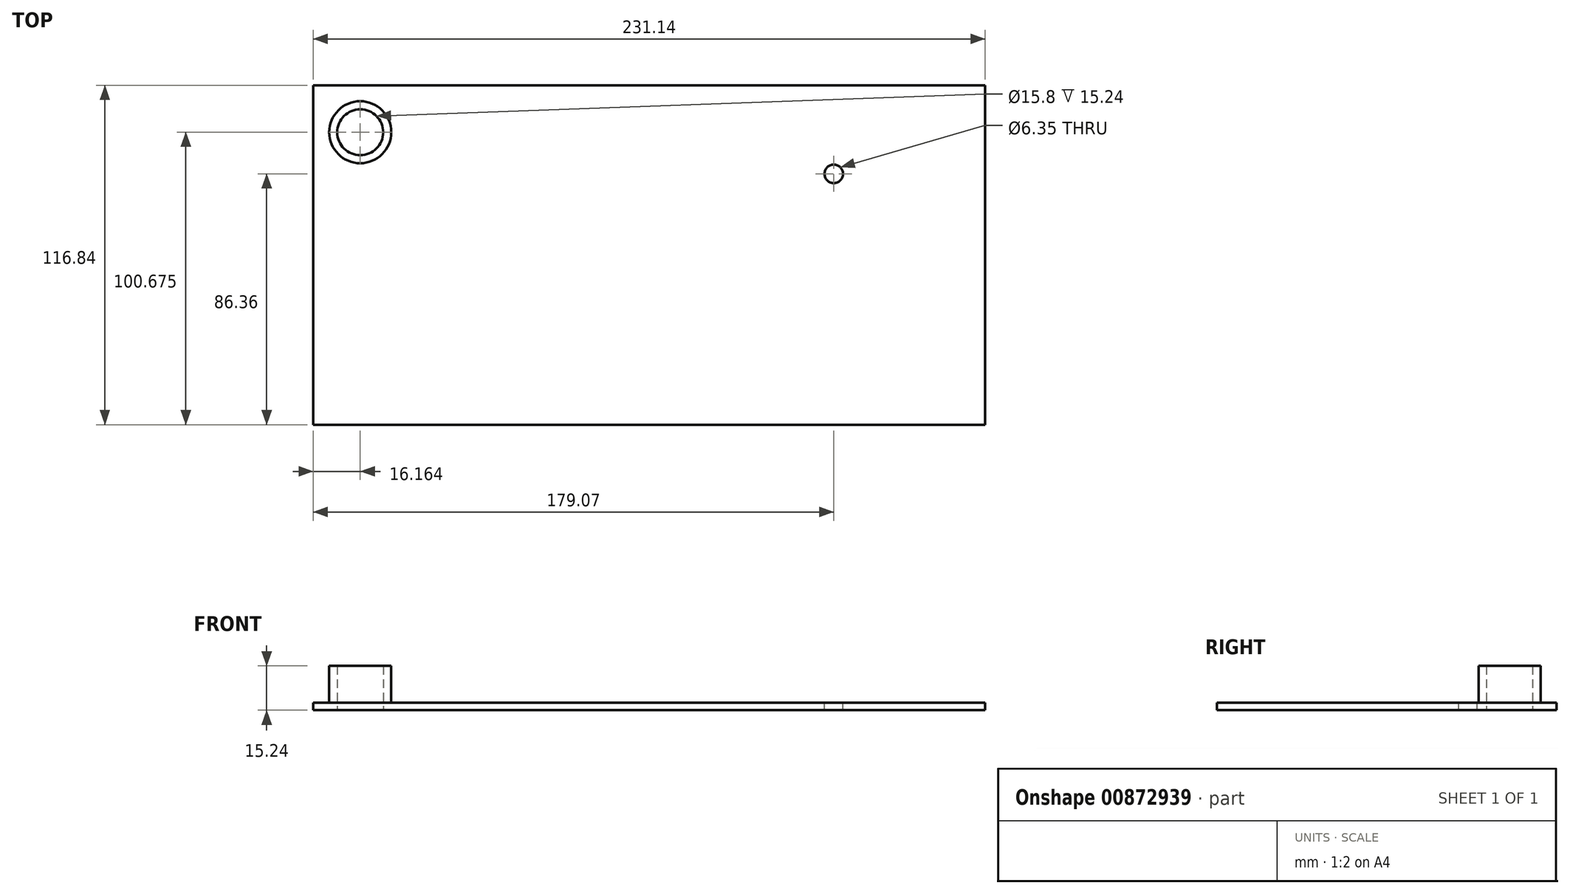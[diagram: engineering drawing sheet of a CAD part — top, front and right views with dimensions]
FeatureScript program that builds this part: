
annotation { "Feature Type Name" : "Feature", "Feature Type Description" : "" }
export const myFeature = defineFeature(function(context is Context, id is Id, definition is map)
    precondition{}
    {
        {
            var Q0;
            Q0=qCreatedBy(makeId("Top.planeOp"),FACE);
            var sketch = newSketch(context, id + "F0", { "sketchPlane" : qUnion([Q0])});
            skLineSegment(sketch, "E0.bottom", {"start": v(115.57, 58.42) * mm, "end": v(-115.57, 58.42) * mm});
            skLineSegment(sketch, "E0.top", {"start": v(115.57, -58.42) * mm, "end": v(-115.57, -58.42) * mm});
            skLineSegment(sketch, "E0.left", {"start": v(115.57, 58.42) * mm, "end": v(115.57, -58.42) * mm});
            skLineSegment(sketch, "E0.right", {"start": v(-115.57, 58.42) * mm, "end": v(-115.57, -58.42) * mm});
            skPoint(sketch, "E0.middle", {"position": v(0, 0) * mm});
            skSolve(sketch);
        }
        {
            var Q0;
            Q0=makeQuery(id+"F0.imprint","IMPRINT",FACE,{"disambiguationData":[TD([[makeQuery(id+"F0.imprint","IMPRINT",EDGE,{"derivedFrom":sQuery(id+"F0.wireOp",EDGE,"E0.bottom")}),1.0]])]});
            extrude(context, id + "F1", {"entities" : qUnion([Q0]), "depth" : 2.54 * mm, "offsetDistance" : 25.4 * mm});
        }
        {
            var Q0;
            Q0=makeQuery(id+"F1.opExtrude","CAP_FACE",FACE,{"disambiguationData":[OSD([sQuery(id+"F0.wireOp",EDGE,"E0.bottom"),sQuery(id+"F0.wireOp",EDGE,"E0.top"),sQuery(id+"F0.wireOp",EDGE,"E0.left"),sQuery(id+"F0.wireOp",EDGE,"E0.right")])],"isStart":false});
            var sketch = newSketch(context, id + "F2", { "sketchPlane" : qUnion([Q0])});
            skLineSegment(sketch, "E1", {"start": v(-115.57, 58.42) * mm, "end": v(-99.4, 42.26) * mm});
            skCircle(sketch, "E2", {"center": v(-99.4, 42.26) * mm, "radius": 7.9 * mm});
            skCircle(sketch, "E3", {"center": v(-99.4, 42.26) * mm, "radius": 10.67 * mm});
            skSolve(sketch);
        }
        {
            var Q0;
            Q0=makeQuery(id+"F2.imprint","IMPRINT",FACE,{"disambiguationData":[TD([[makeQuery(id+"F2.imprint","IMPRINT",EDGE,{"derivedFrom":sQuery(id+"F2.wireOp",EDGE,"E2")}),-1.0]])]});
            extrude(context, id + "F3", {"entities" : qUnion([Q0]), "operationType" : NewBodyOperationType.ADD, "depth" : 12.7 * mm, "offsetDistance" : 25.4 * mm});
        }
        {
            var Q0;
            Q0=makeQuery(id+"F3.boolean.opBoolean","SPLIT",FACE,{"disambiguationData":[TD([makeQuery(id+"F3.opExtrude","SWEPT_FACE",FACE,{"disambiguationData":[OSD([sQuery(id+"F2.wireOp",EDGE,"E2")])]})])],"derivedFrom":makeQuery(id+"F1.opExtrude","CAP_FACE",FACE,{"disambiguationData":[OSD([sQuery(id+"F0.wireOp",EDGE,"E0.bottom"),sQuery(id+"F0.wireOp",EDGE,"E0.top"),sQuery(id+"F0.wireOp",EDGE,"E0.left"),sQuery(id+"F0.wireOp",EDGE,"E0.right")])],"isStart":false})});
            var sketch = newSketch(context, id + "F4", { "sketchPlane" : qUnion([Q0])});
            skCircle(sketch, "E4", {"center": v(-99.4, 42.26) * mm, "radius": 7.9 * mm});
            skSolve(sketch);
        }
        {
            var Q0;
            Q0=makeQuery(id+"F4.imprint","IMPRINT",FACE,{"disambiguationData":[TD([[makeQuery(id+"F4.imprint","IMPRINT",EDGE,{"derivedFrom":sQuery(id+"F4.wireOp",EDGE,"E4")}),1.0]])]});
            var Q1;
            Q1=makeQuery(id+"F1.opExtrude","CAP_FACE",FACE,{"disambiguationData":[OSD([sQuery(id+"F0.wireOp",EDGE,"E0.bottom"),sQuery(id+"F0.wireOp",EDGE,"E0.top"),sQuery(id+"F0.wireOp",EDGE,"E0.left"),sQuery(id+"F0.wireOp",EDGE,"E0.right")])],"isStart":true});
            extrude(context, id + "F5", {"entities" : qUnion([Q0]), "operationType" : NewBodyOperationType.REMOVE, "endBound" : BoundingType.UP_TO_SURFACE, "oppositeDirection" : true, "depth" : 25.4 * mm, "endBoundEntityFace" : qUnion([Q1]), "offsetDistance" : 25.4 * mm});
        }
        {
            var Q0;
            {var subQ0=sQuery(id+"F0.wireOp",EDGE,"E0.left");var subQ4=sQuery(id+"F0.wireOp",EDGE,"E0.top");var subQ6=sQuery(id+"F0.wireOp",EDGE,"E0.right");var subQ8=sQuery(id+"F0.wireOp",EDGE,"E0.bottom");var subQ9=makeQuery(id+"F1.opExtrude","SWEPT_FACE",FACE,{"disambiguationData":[OSD([subQ8])]});Q0=makeQuery(id+"FYuy4ss7uEAQiOW_1.1.F3.boolean.opBoolean","SPLIT",FACE,{"disambiguationData":[TD([subQ9])],"derivedFrom":makeQuery(id+"F3.boolean.opBoolean","SPLIT",FACE,{"disambiguationData":[TD([subQ9])],"derivedFrom":makeQuery(id+"F1.opExtrude","CAP_FACE",FACE,{"disambiguationData":[OSD([subQ8,subQ4,subQ0,subQ6])],"isStart":false})})});}
            var sketch = newSketch(context, id + "F6", { "sketchPlane" : qUnion([Q0])});
            skLineSegment(sketch, "E5.bottom", {"start": v(41, 52.94) * mm, "end": v(-41, 52.94) * mm});
            skLineSegment(sketch, "E5.top", {"start": v(41, 2.94) * mm, "end": v(-41, 2.94) * mm});
            skLineSegment(sketch, "E5.left", {"start": v(41, 52.94) * mm, "end": v(41, 2.94) * mm});
            skLineSegment(sketch, "E5.right", {"start": v(-41, 52.94) * mm, "end": v(-41, 2.94) * mm});
            skPoint(sketch, "E5.middle", {"position": v(0, 27.94) * mm});
            skSolve(sketch);
        }
        {
            var Q0;
            Q0=makeQuery(id+"F6.imprint","IMPRINT",FACE,{"disambiguationData":[TD([[makeQuery(id+"F6.imprint","IMPRINT",EDGE,{"derivedFrom":sQuery(id+"F6.wireOp",EDGE,"E5.bottom")}),-1.0]])]});
            var sketch = newSketch(context, id + "F7", { "sketchPlane" : qUnion([Q0])});
            skLineSegment(sketch, "E6", {"start": v(0, 0) * mm, "end": v(0, 27.94) * mm});
            skLineSegment(sketch, "E7", {"start": v(0, 27.94) * mm, "end": v(63.5, 27.94) * mm});
            skCircle(sketch, "E8", {"center": v(63.5, 27.94) * mm, "radius": 3.18 * mm});
            skSolve(sketch);
        }
        {
            var Q0;
            Q0=makeQuery(id+"F7.imprint","IMPRINT",FACE,{"disambiguationData":[TD([[makeQuery(id+"F7.imprint","IMPRINT",EDGE,{"derivedFrom":sQuery(id+"F7.wireOp",EDGE,"E8")}),1.0]])]});
            var Q1;
            Q1=makeQuery(id+"F1.opExtrude","CAP_FACE",FACE,{"disambiguationData":[OSD([sQuery(id+"F0.wireOp",EDGE,"E0.bottom"),sQuery(id+"F0.wireOp",EDGE,"E0.top"),sQuery(id+"F0.wireOp",EDGE,"E0.left"),sQuery(id+"F0.wireOp",EDGE,"E0.right")])],"isStart":true});
            extrude(context, id + "F8", {"entities" : qUnion([Q0]), "operationType" : NewBodyOperationType.REMOVE, "endBound" : BoundingType.UP_TO_SURFACE, "oppositeDirection" : true, "depth" : 25.4 * mm, "endBoundEntityFace" : qUnion([Q1]), "offsetDistance" : 25.4 * mm});
        }
    });
